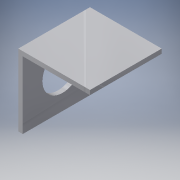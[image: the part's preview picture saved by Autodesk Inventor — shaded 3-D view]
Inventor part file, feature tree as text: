
AUTODESK INVENTOR PART (.ipt)
format: ipt  version: 2016 (Build 200138000, 138)  size: 106,496 bytes
history: native  units: in
note: dims shown in document units (in); Inventor stores cm internally (conversion verified against a paired STEP export)
features: extrude x2, sketch x2
ambient origin geometry x8: Origin, YZ Plane, XZ Plane, XY Plane, X Axis, Y Axis, Z Axis, Center Point
bodies: Solid1 (feature_tree)
feature tree (4):
  extrude  "Extrusion1"  Depth=2.0in
  extrude  "Extrusion2"  Depth=0.125in
  sketch  "Sketch1"  dims[d0=2.0in d1=2.0in]
  sketch  "Sketch2"  dims[d2=0.125in d3=0.125in d4=2.0in d5=0.0in d6=1.0in d7=1.0in d8=1.125in d9=2.0in d10=0.0in]
